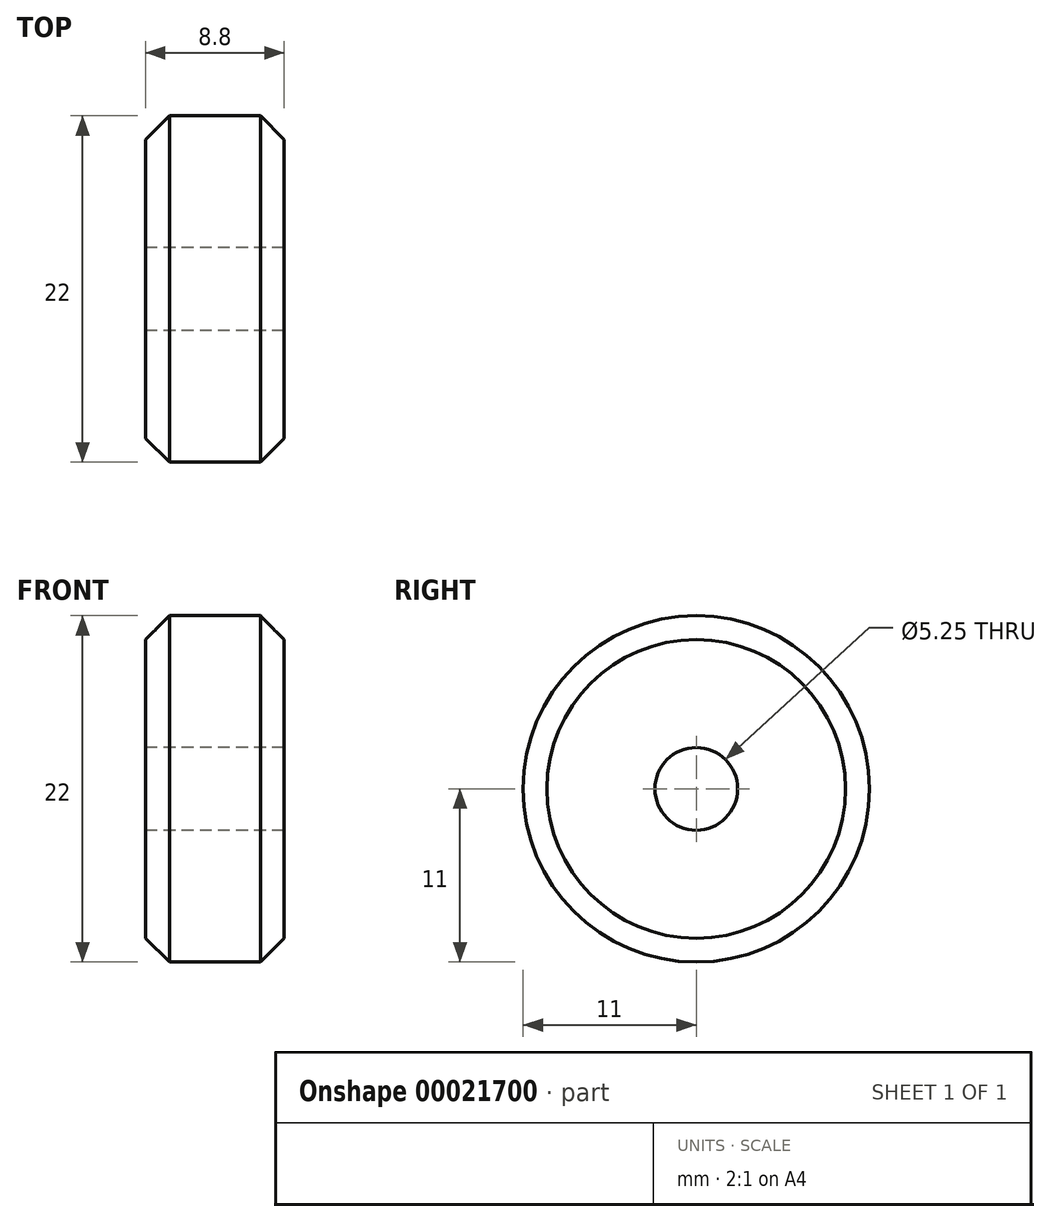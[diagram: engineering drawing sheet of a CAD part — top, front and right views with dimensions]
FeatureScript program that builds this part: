
annotation { "Feature Type Name" : "Feature", "Feature Type Description" : "" }
export const myFeature = defineFeature(function(context is Context, id is Id, definition is map)
    precondition{}
    {
        {
            var Q0;
            Q0=qCreatedBy(makeId("Top.planeOp"),FACE);
            var sketch = newSketch(context, id + "F0", { "sketchPlane" : qUnion([Q0])});
            skLineSegment(sketch, "E0.bottom", {"start": v(0, 0) * mm, "end": v(4.4, 0) * mm, "construction": true});
            skLineSegment(sketch, "E1.bottom", {"start": v(0, 2.62) * mm, "end": v(4.4, 2.62) * mm});
            skLineSegment(sketch, "E1.top", {"start": v(0, 11) * mm, "end": v(2.89, 11) * mm});
            skLineSegment(sketch, "E1.left", {"start": v(0, 2.63) * mm, "end": v(0, 11) * mm, "construction": true});
            skLineSegment(sketch, "E1.right", {"start": v(4.4, 2.63) * mm, "end": v(4.4, 9.48) * mm});
            skLineSegment(sketch, "E2", {"start": v(4.4, 9.48) * mm, "end": v(2.89, 11) * mm});
            skPoint(sketch, "E3.orphan", {"position": v(4.4, 11) * mm});
            skLineSegment(sketch, "E4", {"start": v(0, 2.62) * mm, "end": v(0, 0) * mm, "construction": true});
            skLineSegment(sketch, "E5.MirrorCS", {"start": v(0, 11) * mm, "end": v(-2.89, 11) * mm});
            skLineSegment(sketch, "E6.MirrorCS", {"start": v(-4.4, 9.48) * mm, "end": v(-2.89, 11) * mm});
            skLineSegment(sketch, "E7.MirrorCS", {"start": v(-4.4, 2.63) * mm, "end": v(-4.4, 9.48) * mm});
            skLineSegment(sketch, "E8.MirrorCS", {"start": v(0, 2.62) * mm, "end": v(-4.4, 2.62) * mm});
            skSolve(sketch);
        }
        {
            var Q0;
            Q0=makeQuery(id+"F0.imprint","IMPRINT",FACE,{"disambiguationData":[TD([[makeQuery(id+"F0.imprint","IMPRINT",EDGE,{"derivedFrom":sQuery(id+"F0.wireOp",EDGE,"E1.top")}),-1.0]])]});
            var Q1;
            Q1=sQuery(id+"F0.wireOp",EDGE,"E0.bottom");
            revolve(context, id + "F1", {"entities" : qUnion([Q0]), "axis" : qUnion([Q1]), "revolveType" : RevolveType.FULL});
        }
    });
